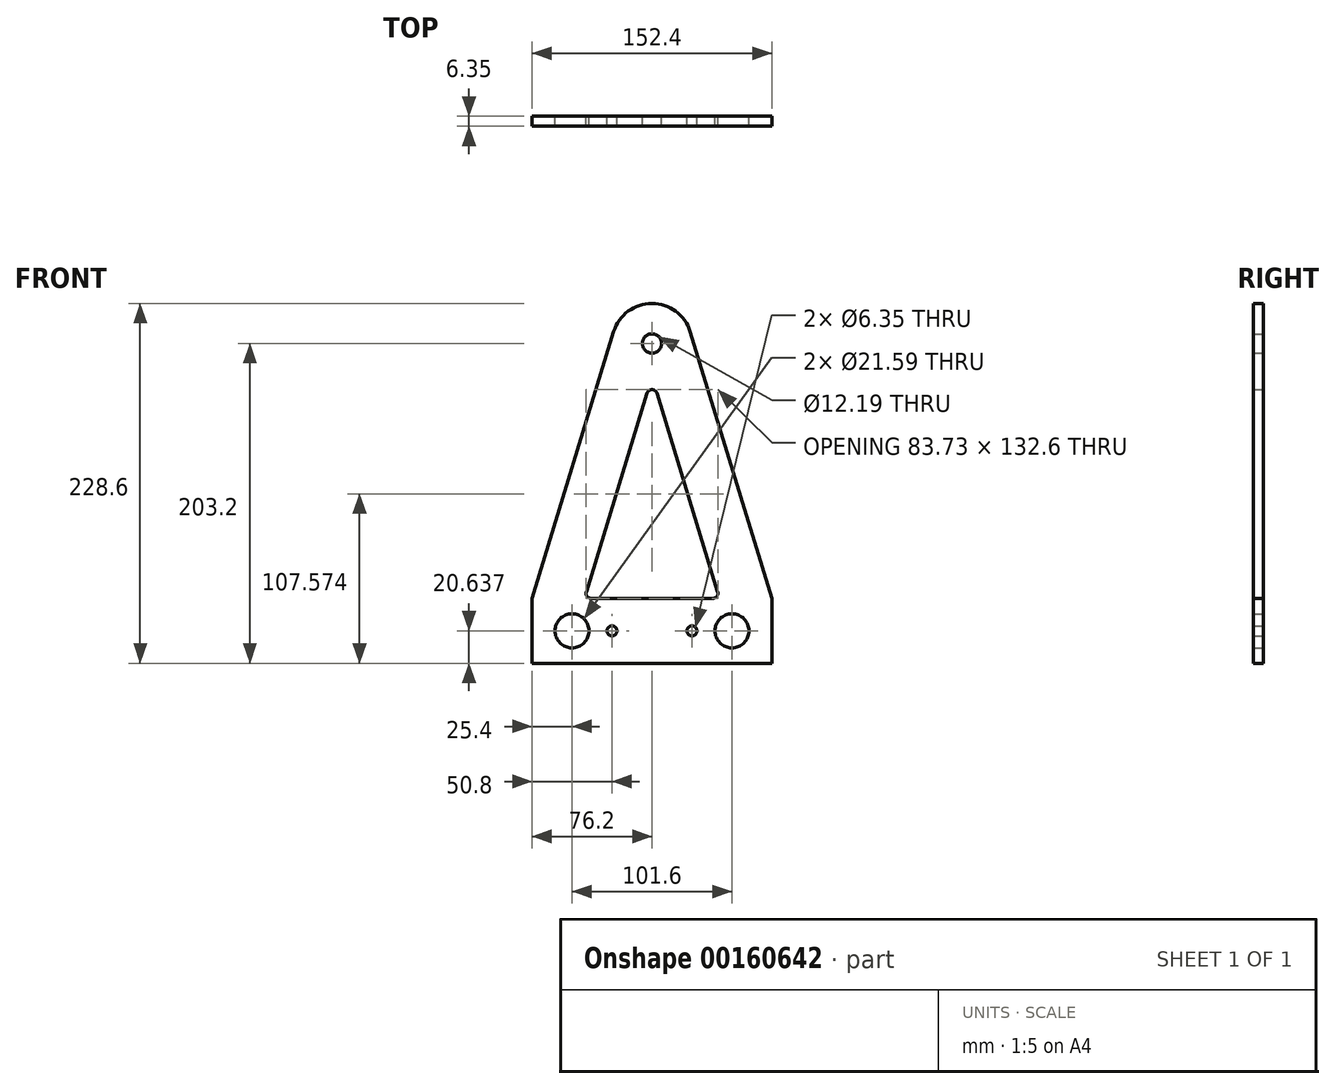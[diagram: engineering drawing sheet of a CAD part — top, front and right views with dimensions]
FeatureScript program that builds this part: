
annotation { "Feature Type Name" : "Feature", "Feature Type Description" : "" }
export const myFeature = defineFeature(function(context is Context, id is Id, definition is map)
    precondition{}
    {
        {
            var Q0;
            Q0=qCreatedBy(makeId("Front.planeOp"),FACE);
            var sketch = newSketch(context, id + "F0", { "sketchPlane" : qUnion([Q0])});
            skLineSegment(sketch, "E0", {"start": v(0, 0) * mm, "end": v(-152.4, 0) * mm});
            skLineSegment(sketch, "E1", {"start": v(-152.4, 0) * mm, "end": v(-152.4, 203.2) * mm, "construction": true});
            skLineSegment(sketch, "E2", {"start": v(0, 0) * mm, "end": v(0, 203.2) * mm, "construction": true});
            skLineSegment(sketch, "E3", {"start": v(-152.4, 0) * mm, "end": v(-152.4, 41.27) * mm});
            skLineSegment(sketch, "E4", {"start": v(0, 0) * mm, "end": v(0, 41.28) * mm});
            skLineSegment(sketch, "E5", {"start": v(-152.4, 41.28) * mm, "end": v(-100.48, 210.64) * mm});
            skLineSegment(sketch, "E6", {"start": v(-51.92, 210.64) * mm, "end": v(0, 41.27) * mm});
            skPoint(sketch, "E7", {"position": v(-76.2, 0) * mm});
            skPoint(sketch, "E8.visualSharp", {"position": v(-76.2, 289.87) * mm});
            skArc(sketch, "E8.filletArc", {"start": v(-51.92, 210.64) * mm, "mid": v(-76.2, 228.6) * mm, "end": v(-100.48, 210.64) * mm});
            skLineSegment(sketch, "E9", {"start": v(-114.9, 41.28) * mm, "end": v(-37.5, 41.28) * mm});
            skLineSegment(sketch, "E10", {"start": v(-34.47, 45.38) * mm, "end": v(-73.16, 171.63) * mm});
            skLineSegment(sketch, "E11", {"start": v(-79.24, 171.63) * mm, "end": v(-117.93, 45.38) * mm});
            skPoint(sketch, "E12.visualSharp", {"position": v(-119.2, 41.28) * mm});
            skArc(sketch, "E12.filletArc", {"start": v(-117.93, 45.38) * mm, "mid": v(-117.45, 42.56) * mm, "end": v(-114.9, 41.28) * mm});
            skPoint(sketch, "E13.visualSharp", {"position": v(-33.2, 41.28) * mm});
            skArc(sketch, "E13.filletArc", {"start": v(-37.5, 41.28) * mm, "mid": v(-34.95, 42.56) * mm, "end": v(-34.47, 45.38) * mm});
            skPoint(sketch, "E14.visualSharp", {"position": v(-76.2, 181.53) * mm});
            skArc(sketch, "E14.filletArc", {"start": v(-73.16, 171.63) * mm, "mid": v(-76.2, 173.87) * mm, "end": v(-79.24, 171.63) * mm});
            skPoint(sketch, "E15", {"position": v(-152.4, 20.64) * mm});
            skPoint(sketch, "E16", {"position": v(0, 20.64) * mm});
            skCircle(sketch, "E17", {"center": v(-127, 20.64) * mm, "radius": 10.8 * mm});
            skCircle(sketch, "E18", {"center": v(-25.4, 20.64) * mm, "radius": 10.8 * mm});
            skCircle(sketch, "E19", {"center": v(-101.6, 20.64) * mm, "radius": 3.18 * mm});
            skCircle(sketch, "E20", {"center": v(-50.8, 20.64) * mm, "radius": 3.18 * mm});
            skLineSegment(sketch, "E21", {"start": v(-127, 20.64) * mm, "end": v(-25.4, 20.64) * mm, "construction": true});
            skPoint(sketch, "E22", {"position": v(-76.2, 20.64) * mm});
            skCircle(sketch, "E23", {"center": v(-76.2, 203.2) * mm, "radius": 6.1 * mm});
            skSolve(sketch);
        }
        {
            var Q0;
            Q0 = qSketchRegion(id + "F0", true);
            extrude(context, id + "F1", {"entities" : qUnion([Q0]), "depth" : 6.35 * mm});
        }
    });
